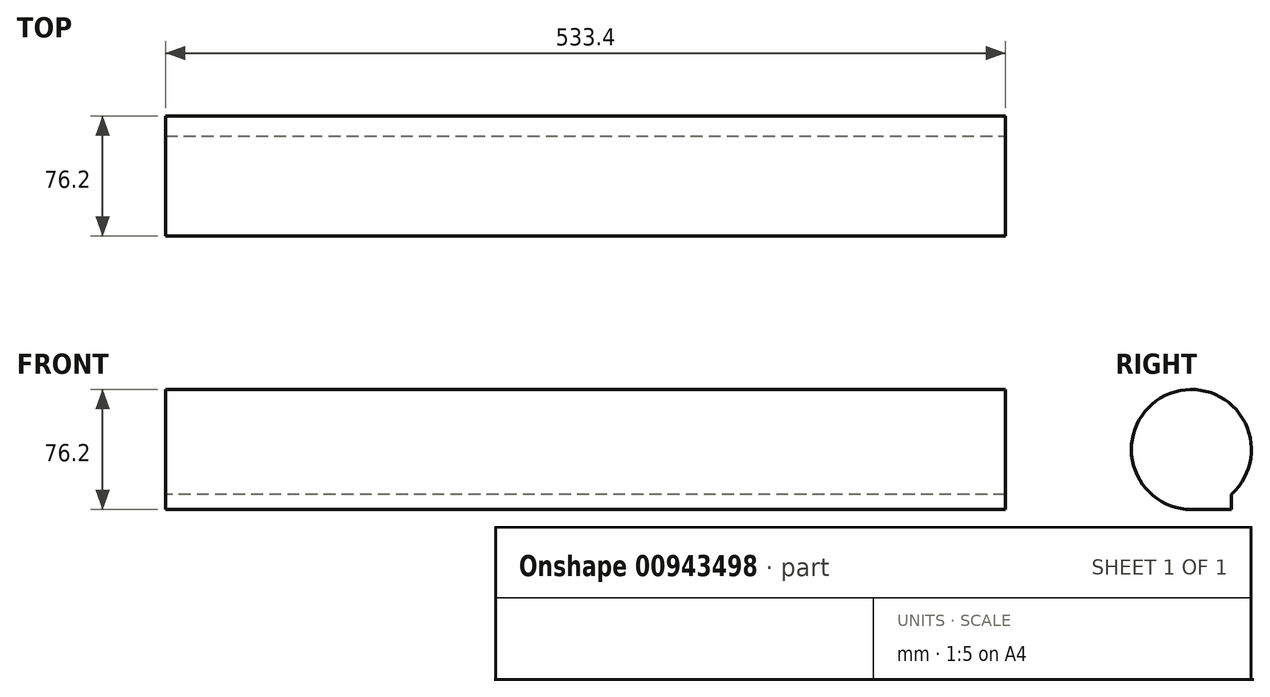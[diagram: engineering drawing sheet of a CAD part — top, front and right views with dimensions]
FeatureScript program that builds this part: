
annotation { "Feature Type Name" : "Feature", "Feature Type Description" : "" }
export const myFeature = defineFeature(function(context is Context, id is Id, definition is map)
    precondition{}
    {
        {
            var Q0;
            Q0=qCreatedBy(makeId("Front.planeOp"),FACE);
            var sketch = newSketch(context, id + "F0", { "sketchPlane" : qUnion([Q0])});
            skLineSegment(sketch, "E0.bottom", {"start": v(-271.23, 38.1) * mm, "end": v(262.17, 38.1) * mm});
            skLineSegment(sketch, "E0.top", {"start": v(-271.23, 0) * mm, "end": v(262.17, 0) * mm});
            skLineSegment(sketch, "E0.left", {"start": v(-271.23, 38.1) * mm, "end": v(-271.23, 0) * mm});
            skLineSegment(sketch, "E0.right", {"start": v(262.17, 38.1) * mm, "end": v(262.17, 0) * mm});
            skSolve(sketch);
        }
        {
            var Q0;
            Q0 = qSketchRegion(id + "F0", true);
            extrude(context, id + "F1", {"entities" : qUnion([Q0]), "depth" : 25.4 * mm, "offsetDistance" : 25.4 * mm});
        }
        {
            var Q0;
            Q0=makeQuery(id+"F1.opExtrude","CAP_FACE",FACE,{"disambiguationData":[OSD([sQuery(id+"F0.wireOp",EDGE,"E0.bottom"),sQuery(id+"F0.wireOp",EDGE,"E0.top"),sQuery(id+"F0.wireOp",EDGE,"E0.left"),sQuery(id+"F0.wireOp",EDGE,"E0.right")])],"isStart":false});
            var Q1;
            Q1=makeQuery(id+"F1.opExtrude","CAP_EDGE",EDGE,{"disambiguationData":[OSD([sQuery(id+"F0.wireOp",EDGE,"E0.bottom")])],"isStart":false});
            revolve(context, id + "F2", {"operationType" : NewBodyOperationType.ADD, "surfaceOperationType" : NewSurfaceOperationType.NEW, "entities" : qUnion([Q0]), "axis" : qUnion([Q1]), "revolveType" : RevolveType.FULL});
        }
    });
